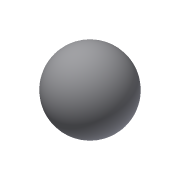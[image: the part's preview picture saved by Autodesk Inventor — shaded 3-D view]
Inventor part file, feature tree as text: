
AUTODESK INVENTOR PART (.ipt)
format: ipt  version: 2019.4 (Build 234330000, 330)  size: 103,936 bytes
history: native  units: mm
features: revolve x1, sketch x1
ambient origin geometry x8: Origin, YZ Plane, XZ Plane, XY Plane, X Axis, Y Axis, Z Axis, Center Point
bodies: Solid1 (feature_tree)
feature tree (2):
  revolve  "Revolution1"  Angle=90.0deg
  sketch  "Sketch1"  dims[d0=2.0mm d1=90.0deg]
